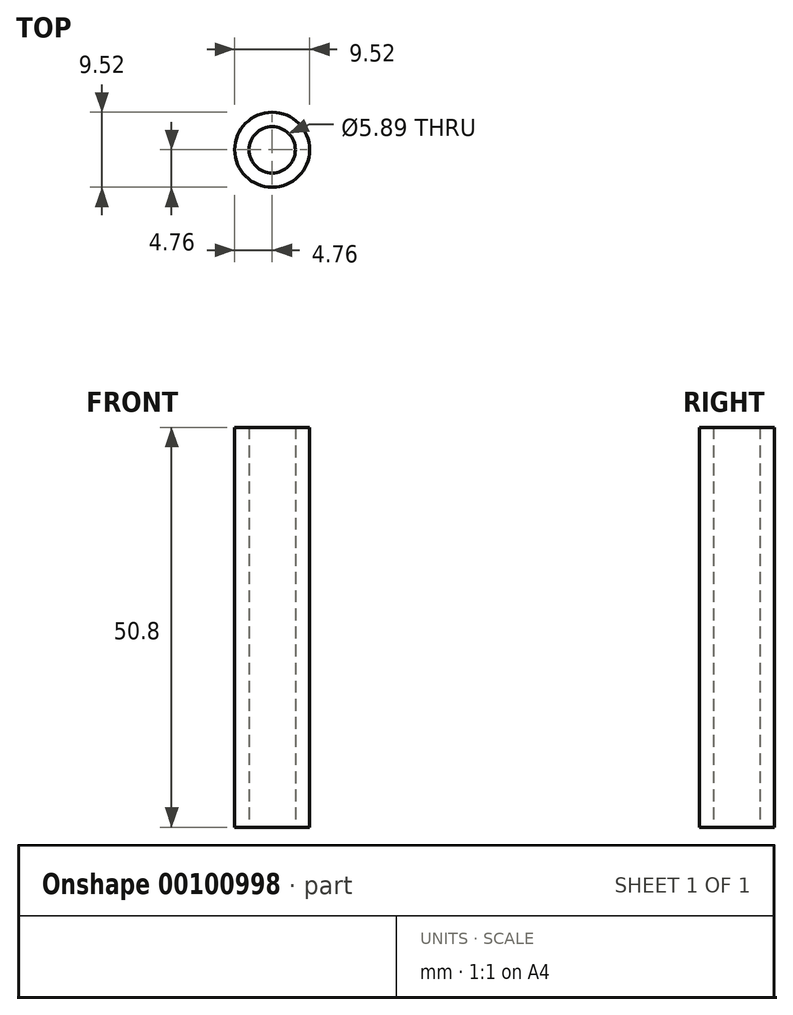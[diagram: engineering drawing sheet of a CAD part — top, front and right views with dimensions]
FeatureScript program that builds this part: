
annotation { "Feature Type Name" : "Feature", "Feature Type Description" : "" }
export const myFeature = defineFeature(function(context is Context, id is Id, definition is map)
    precondition{}
    {
        {
            var Q0;
            Q0=qCreatedBy(makeId("Top.planeOp"),FACE);
            var sketch = newSketch(context, id + "F0", { "sketchPlane" : qUnion([Q0])});
            skCircle(sketch, "E0", {"center": v(0, 0) * mm, "radius": 4.76 * mm});
            skCircle(sketch, "E1", {"center": v(0, 0) * mm, "radius": 2.95 * mm});
            skSolve(sketch);
        }
        {
            var Q0;
            Q0 = qSketchRegion(id + "F0", true);
            extrude(context, id + "F1", {"entities" : qUnion([Q0]), "depth" : 50.8 * mm});
        }
    });
